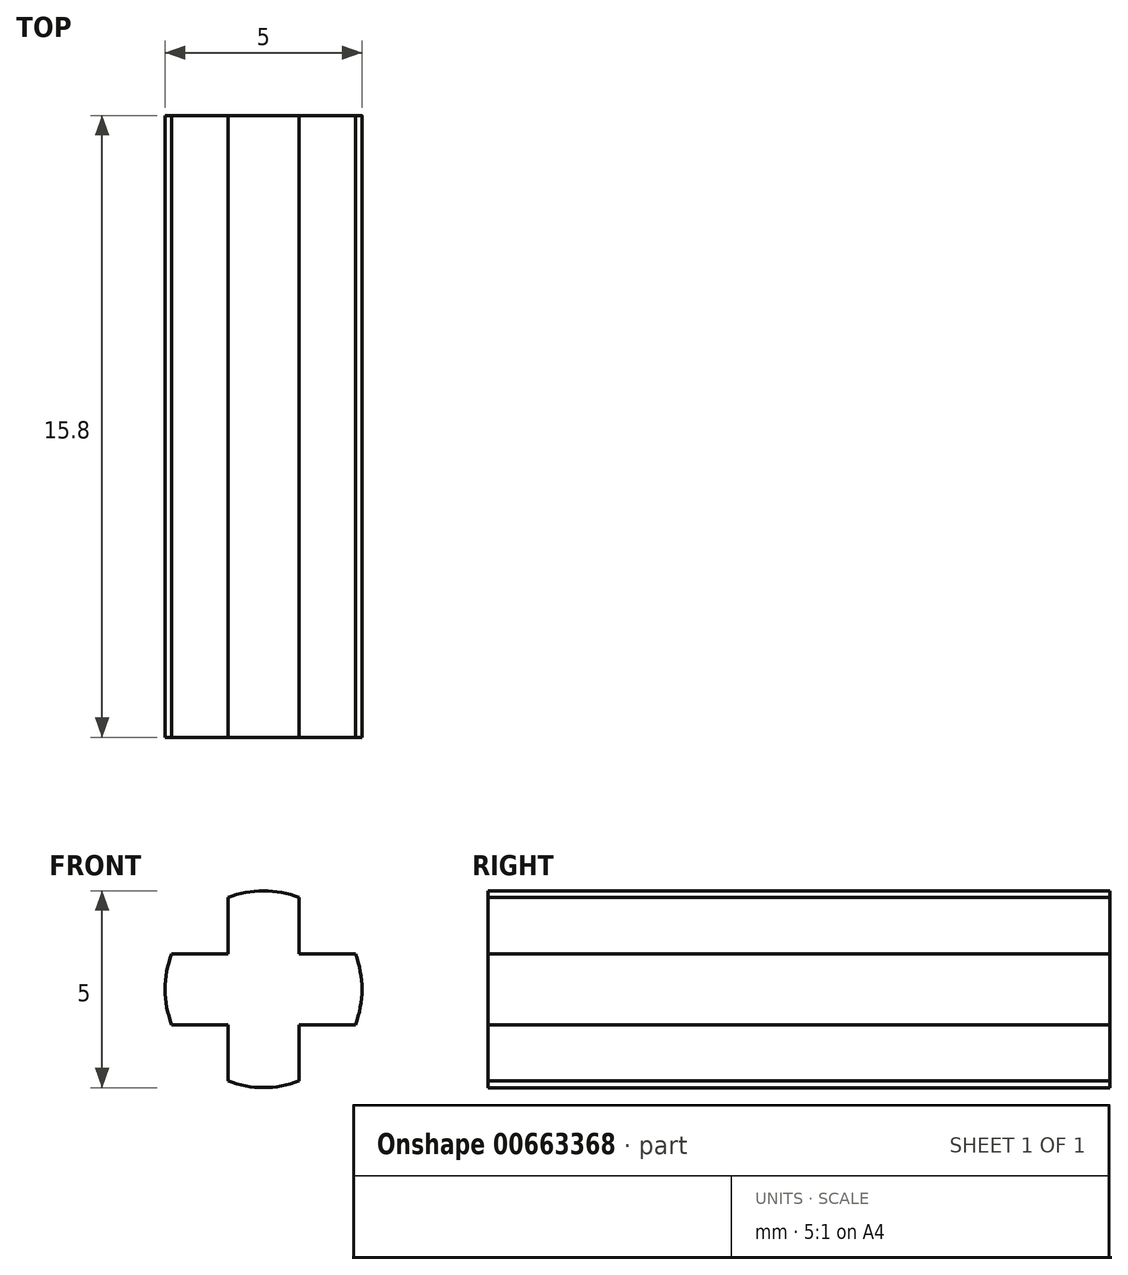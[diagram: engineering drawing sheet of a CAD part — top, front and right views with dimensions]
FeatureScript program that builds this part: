
annotation { "Feature Type Name" : "Feature", "Feature Type Description" : "" }
export const myFeature = defineFeature(function(context is Context, id is Id, definition is map)
    precondition{}
    {
        {
            var Q0;
            Q0=qCreatedBy(makeId("Front.planeOp"),FACE);
            var sketch = newSketch(context, id + "F0", { "sketchPlane" : qUnion([Q0])});
            skLineSegment(sketch, "E0.left", {"start": v(0.9, 2.33) * mm, "end": v(0.9, -2.33) * mm});
            skLineSegment(sketch, "E0.right", {"start": v(-0.9, 2.33) * mm, "end": v(-0.9, -2.33) * mm});
            skPoint(sketch, "E0.middle", {"position": v(0, 0) * mm});
            skLineSegment(sketch, "E1.bottom", {"start": v(2.33, 0.9) * mm, "end": v(-2.33, 0.9) * mm});
            skLineSegment(sketch, "E1.top", {"start": v(2.33, -0.9) * mm, "end": v(-2.33, -0.9) * mm});
            skArc(sketch, "E2", {"start": v(-0.9, -2.33) * mm, "mid": v(0, -2.5) * mm, "end": v(0.9, -2.33) * mm});
            skArc(sketch, "E3.trimOffspring", {"start": v(-2.33, 0.9) * mm, "mid": v(-2.5, 0) * mm, "end": v(-2.33, -0.9) * mm});
            skArc(sketch, "E4.trimOffspring", {"start": v(0.9, 2.33) * mm, "mid": v(0, 2.5) * mm, "end": v(-0.9, 2.33) * mm});
            skArc(sketch, "E5.trimOffspring", {"start": v(2.33, -0.9) * mm, "mid": v(2.5, 0) * mm, "end": v(2.33, 0.9) * mm});
            skSolve(sketch);
        }
        {
            var Q0;
            Q0=qSketchRegion(id+"F0",true);
            extrude(context, id + "F1", {"entities" : qUnion([Q0]), "endBound" : BoundingType.SYMMETRIC, "depth" : 15.8 * mm, "offsetDistance" : 25 * mm});
        }
    });
